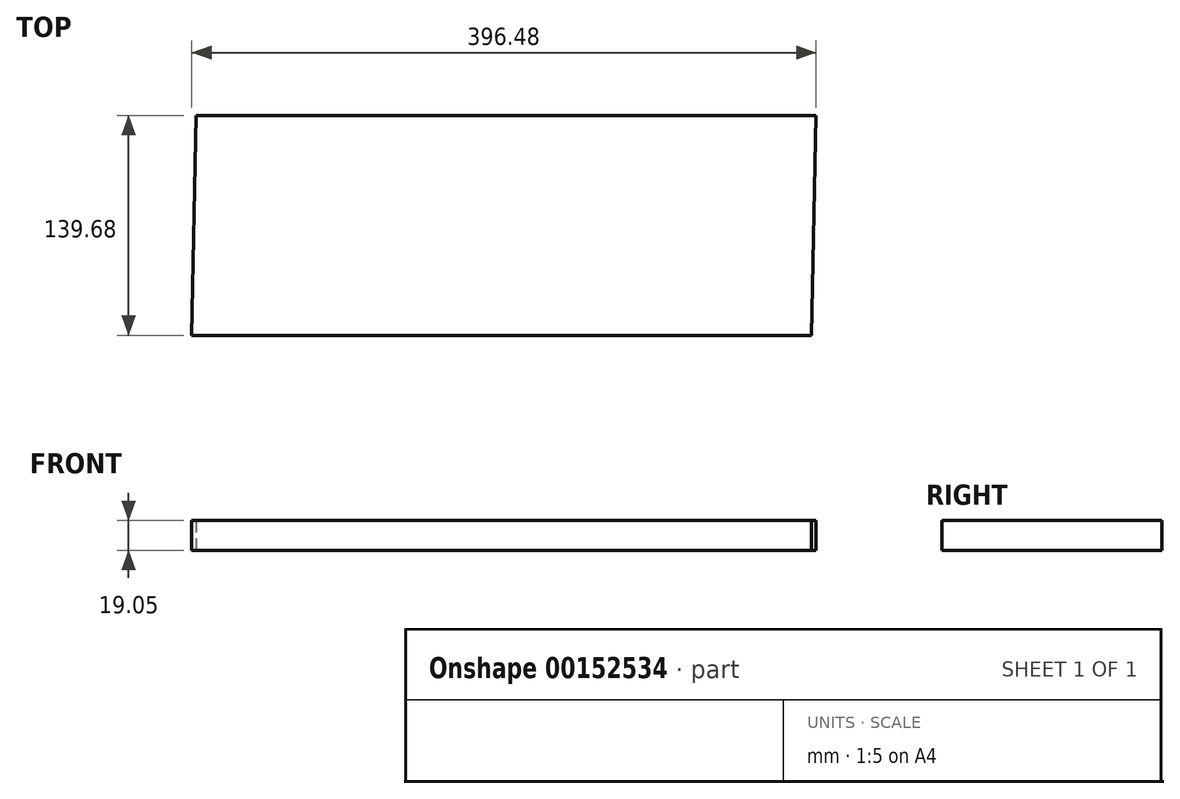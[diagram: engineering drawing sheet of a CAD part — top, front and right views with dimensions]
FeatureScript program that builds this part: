
annotation { "Feature Type Name" : "Feature", "Feature Type Description" : "" }
export const myFeature = defineFeature(function(context is Context, id is Id, definition is map)
    precondition{}
    {
        {
            var Q0;
            Q0=qCreatedBy(makeId("Top.planeOp"),FACE);
            var sketch = newSketch(context, id + "F0", { "sketchPlane" : qUnion([Q0])});
            skLineSegment(sketch, "E0", {"start": v(-195.46, 69.84) * mm, "end": v(198.24, 69.84) * mm});
            skLineSegment(sketch, "E1", {"start": v(-198.24, -69.84) * mm, "end": v(195.46, -69.84) * mm});
            skPoint(sketch, "E2", {"position": v(1.4, 69.84) * mm});
            skPoint(sketch, "E3", {"position": v(-1.4, -69.84) * mm});
            skLineSegment(sketch, "E4", {"start": v(1.4, 69.84) * mm, "end": v(-1.4, -69.84) * mm, "construction": true});
            skLineSegment(sketch, "E5", {"start": v(-198.24, -69.84) * mm, "end": v(-195.46, 69.84) * mm});
            skLineSegment(sketch, "E6", {"start": v(195.46, -69.84) * mm, "end": v(198.24, 69.84) * mm});
            skSolve(sketch);
        }
        {
            var Q0;
            Q0 = qSketchRegion(id + "F0", true);
            extrude(context, id + "F1", {"entities" : qUnion([Q0]), "depth" : 19.05 * mm});
        }
    });
